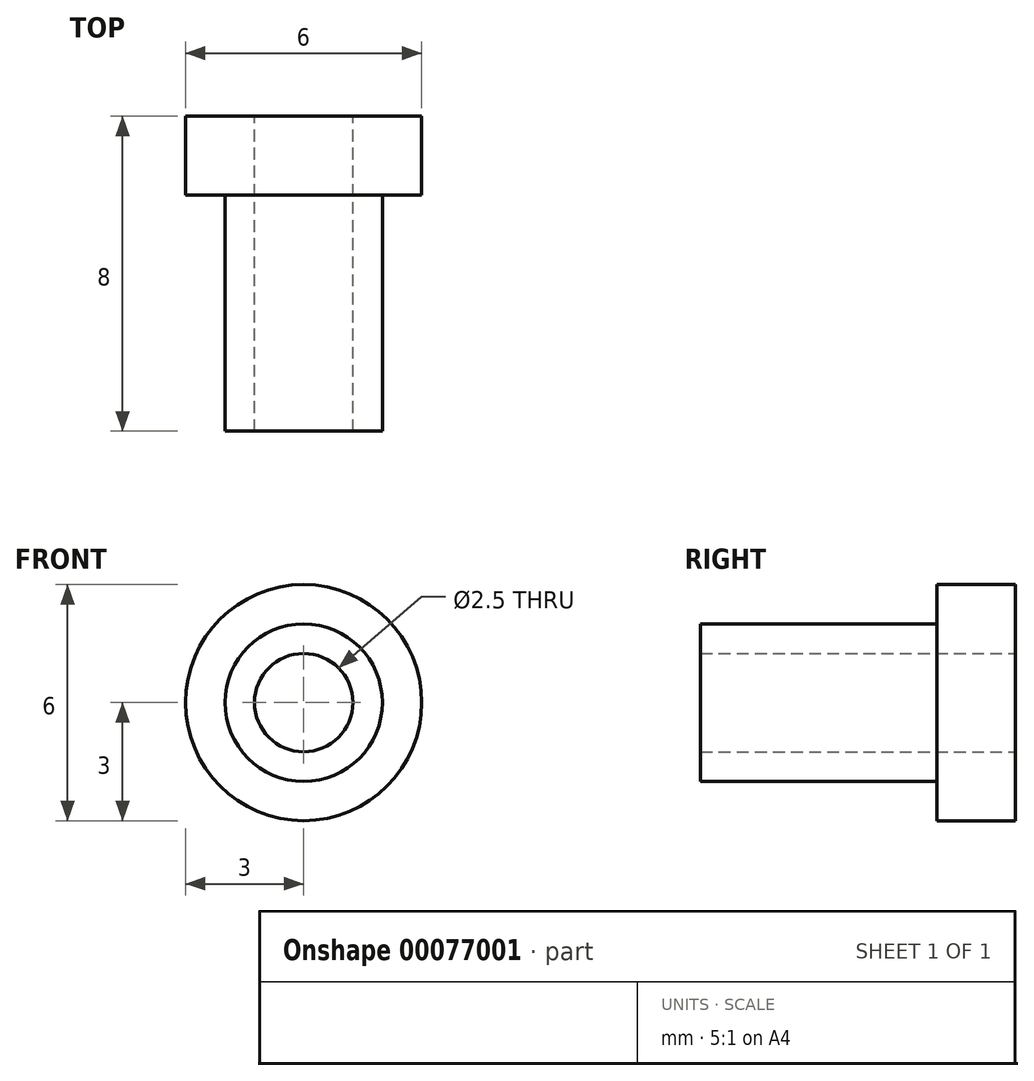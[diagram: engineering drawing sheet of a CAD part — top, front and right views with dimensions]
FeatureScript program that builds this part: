
annotation { "Feature Type Name" : "Feature", "Feature Type Description" : "" }
export const myFeature = defineFeature(function(context is Context, id is Id, definition is map)
    precondition{}
    {
        {
            var Q0;
            Q0=qCreatedBy(makeId("Front.planeOp"),FACE);
            var sketch = newSketch(context, id + "F0", { "sketchPlane" : qUnion([Q0])});
            skCircle(sketch, "E0", {"center": v(0, 0) * mm, "radius": 3 * mm});
            skSolve(sketch);
        }
        {
            var Q0;
            Q0=makeQuery(id+"F0.imprint","IMPRINT",FACE,{"disambiguationData":[TD([[makeQuery(id+"F0.imprint","IMPRINT",EDGE,{"derivedFrom":sQuery(id+"F0.wireOp",EDGE,"E0")}),1.0]])]});
            extrude(context, id + "F1", {"entities" : qUnion([Q0]), "depth" : 2 * mm});
        }
        {
            var Q0;
            Q0=qCreatedBy(makeId("Front.planeOp"),FACE);
            var sketch = newSketch(context, id + "F2", { "sketchPlane" : qUnion([Q0])});
            skCircle(sketch, "E1", {"center": v(0, 0) * mm, "radius": 2 * mm});
            skSolve(sketch);
        }
        {
            var Q0;
            Q0 = qSketchRegion(id + "F2", true);
            extrude(context, id + "F3", {"entities" : qUnion([Q0]), "operationType" : NewBodyOperationType.ADD, "depth" : 8 * mm});
        }
        {
            var Q0;
            Q0=qCreatedBy(makeId("Front.planeOp"),FACE);
            var sketch = newSketch(context, id + "F4", { "sketchPlane" : qUnion([Q0])});
            skCircle(sketch, "E2", {"center": v(0, 0) * mm, "radius": 1.25 * mm});
            skSolve(sketch);
        }
        {
            var Q0;
            Q0=makeQuery(id+"F4.imprint","IMPRINT",FACE,{"disambiguationData":[TD([[makeQuery(id+"F4.imprint","IMPRINT",EDGE,{"derivedFrom":sQuery(id+"F4.wireOp",EDGE,"E2")}),1.0]])]});
            extrude(context, id + "F5", {"entities" : qUnion([Q0]), "operationType" : NewBodyOperationType.REMOVE, "endBound" : BoundingType.THROUGH_ALL, "depth" : 25 * mm});
        }
    });
